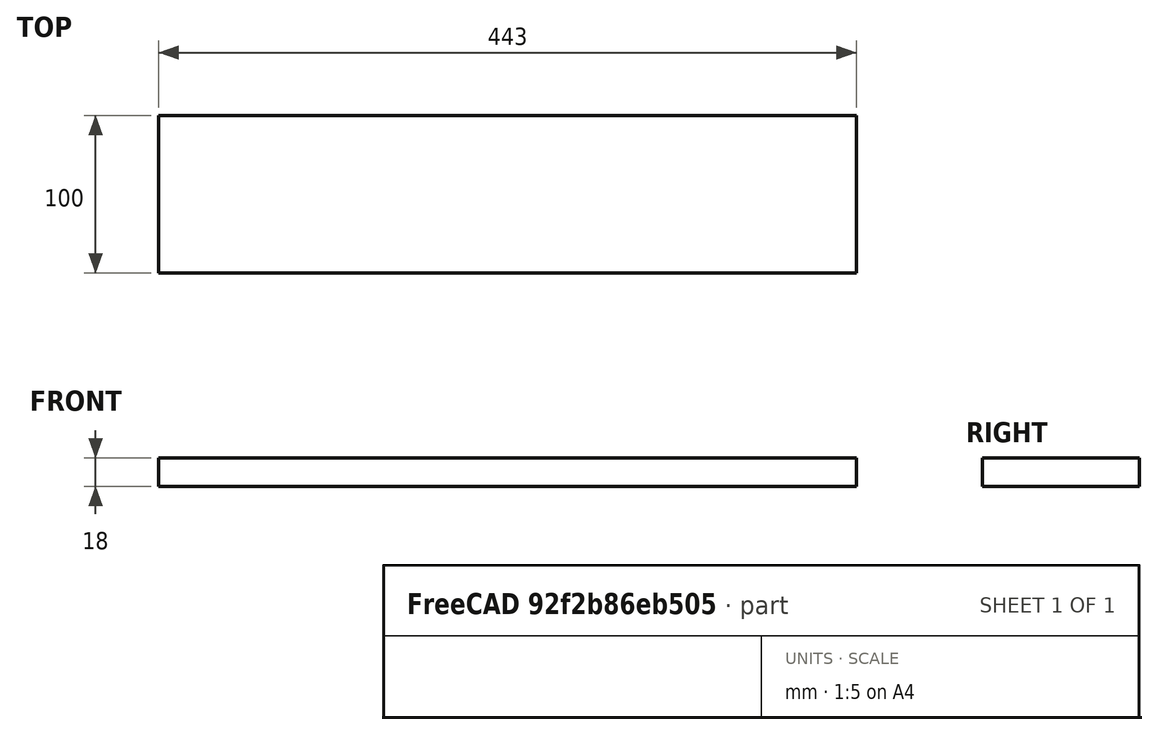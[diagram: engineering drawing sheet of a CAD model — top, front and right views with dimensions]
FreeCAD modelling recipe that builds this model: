
FCSTD DOCUMENT  (FreeCAD 0.17R13541 (Git))
Label: FaceIntermediaire
License: All rights reserved
LicenseURL: http://en.wikipedia.org/wiki/All_rights_reserved
objects: Sketcher::SketchObject×1, PartDesign::Pad×1, PartDesign::Body×1
note: 4 computed .brp shape members not serialized (recipe doc carries the construction recipe); baked Part::Feature solids carry a one-line shape summary decoded from their .brp

FEATURE [Sketcher::SketchObject] Sketch
  MapMode = 5
  Support = -> [XY_Plane]
  sketch-geometry (6):
    g0: LineSegment StartX=-221.5 StartY=50 StartZ=0 EndX=221.5 EndY=50 EndZ=0
    g1: LineSegment StartX=221.5 StartY=50 StartZ=0 EndX=221.5 EndY=-50 EndZ=0
    g2: LineSegment StartX=221.5 StartY=-50 StartZ=0 EndX=-221.5 EndY=-50 EndZ=0
    g3: LineSegment StartX=-221.5 StartY=-50 StartZ=0 EndX=-221.5 EndY=50 EndZ=0
    g4: LineSegment [constr] StartX=-221.5 StartY=50 StartZ=0 EndX=221.5 EndY=-50 EndZ=0
    g5: LineSegment [constr] StartX=-221.5 StartY=-50 StartZ=0 EndX=221.5 EndY=50 EndZ=0
  constraints (16):
    c: Coincident(g0,g1)
    c: Coincident(g1,g2)
    c: Coincident(g2,g3)
    c: Coincident(g3,g0)
    c: Horizontal(g0)
    c: Horizontal(g2)
    c: Vertical(g1)
    c: Vertical(g3)
    c: Coincident(g4,g0)
    c: Coincident(g4,g1)
    c: Coincident(g5,g2)
    c: Coincident(g5,g0)
    c: PointOnObject(g-1,g4)
    c: PointOnObject(g-1,g5)
    c: DistanceX(g0,g0) = 443  'Largeur a'
    c: DistanceY(g3,g3) = 100  'Profondeur'
FEATURE [PartDesign::Pad] Pad
  Length = 18
  Length2 = 100
  Profile = -> Sketch
  Type = 0
FEATURE [PartDesign::Body] Body  label="Face intermediaire"
  Group = -> [Sketch,Pad]
  Origin = -> Origin
  Tip = -> Pad
